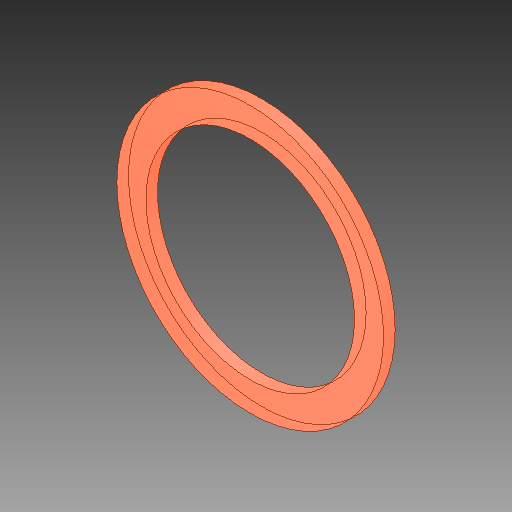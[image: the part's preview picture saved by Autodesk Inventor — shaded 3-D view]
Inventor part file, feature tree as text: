
AUTODESK INVENTOR PART (.ipt)
format: ipt  version: 2019 (Build 230136000, 136)  size: 111,104 bytes
history: native  units: in
note: dims shown in document units (in); Inventor stores cm internally (conversion verified against a paired STEP export)
features: extrude x1, sketch x1
ambient origin geometry x8: Origin, YZ Plane, XZ Plane, XY Plane, X Axis, Y Axis, Z Axis, Center Point
bodies: Solid1 (feature_tree)
feature tree (2):
  extrude  "Extrusion1"  Depth=0.3937in
  sketch  "Sketch1"  dims[d0=7.0866in d1=9.0551in d2=0.3937in d3=0.0in]
